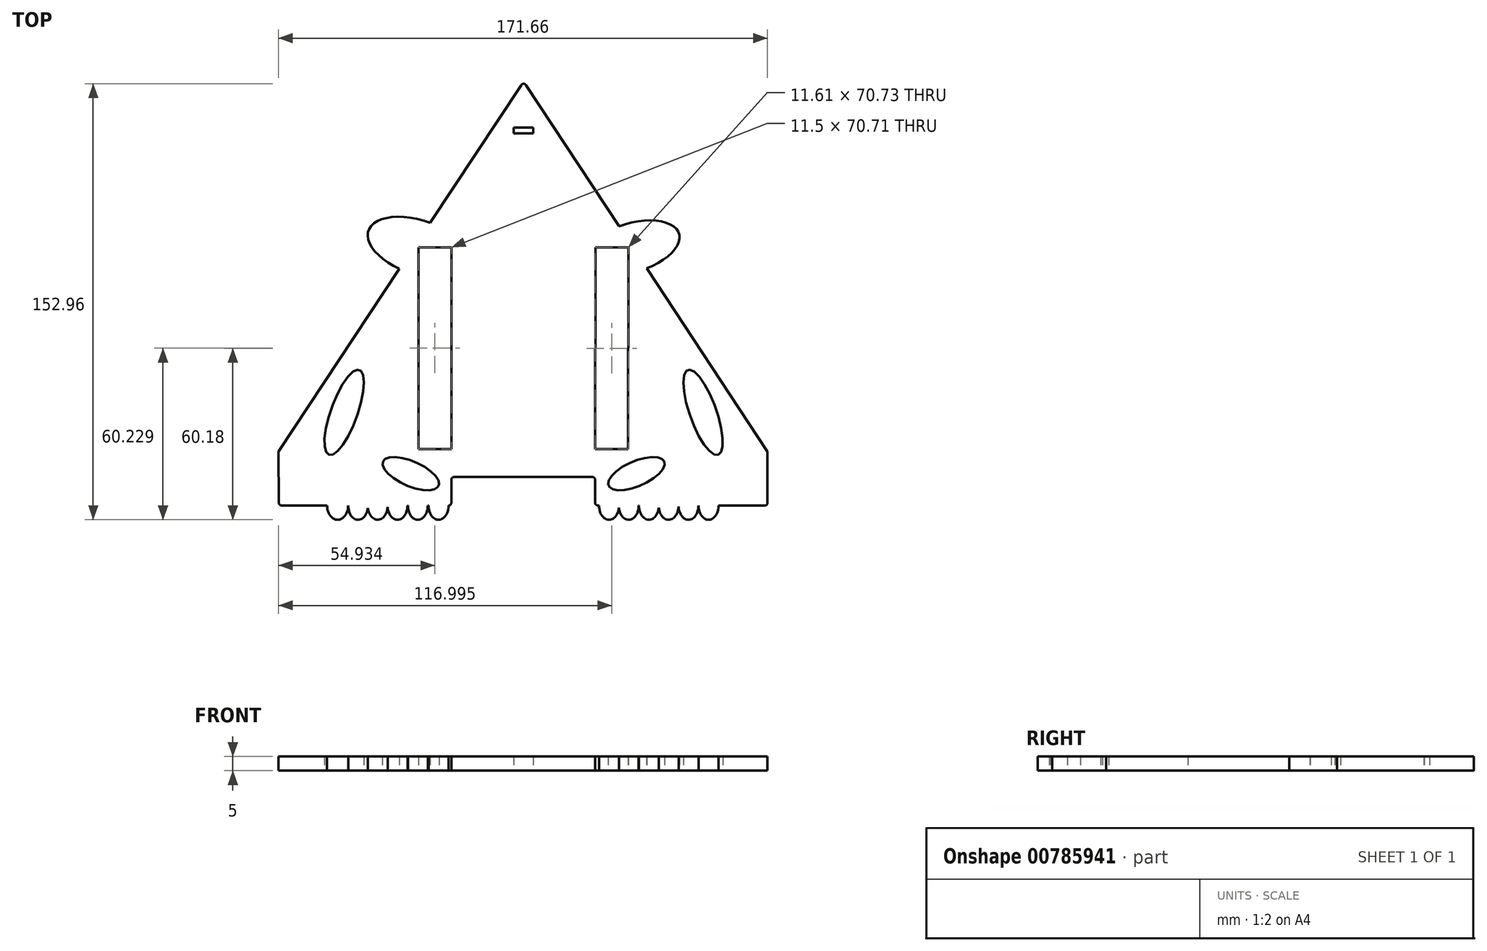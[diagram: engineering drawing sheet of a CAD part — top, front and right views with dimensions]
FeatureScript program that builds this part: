
annotation { "Feature Type Name" : "Feature", "Feature Type Description" : "" }
export const myFeature = defineFeature(function(context is Context, id is Id, definition is map)
    precondition{}
    {
        {
            var Q0;
            Q0=qCreatedBy(makeId("Top.planeOp"),FACE);
            var sketch = newSketch(context, id + "F0", { "sketchPlane" : qUnion([Q0])});
            skPoint(sketch, "E0.0.midPoint", {"position": v(0, -49.5) * mm});
            skPoint(sketch, "E0.cCircle.center.orphan", {"position": v(0, 0) * mm});
            skLineSegment(sketch, "E1", {"start": v(-84.75, -49.5) * mm, "end": v(-54.5, -49.5) * mm});
            skLineSegment(sketch, "E2", {"start": v(84.74, -49.5) * mm, "end": v(26.24, -49.5) * mm});
            skLineSegment(sketch, "E3", {"start": v(25.24, -48.5) * mm, "end": v(25.24, -40.5) * mm});
            skLineSegment(sketch, "E4", {"start": v(24.24, -39.5) * mm, "end": v(-24.24, -39.5) * mm});
            skLineSegment(sketch, "E5", {"start": v(-25.24, -40.5) * mm, "end": v(-25.24, -48.5) * mm});
            skPoint(sketch, "E6.visualSharp", {"position": v(0.12, 99.27) * mm});
            skLineSegment(sketch, "E7", {"start": v(0.95, 98) * mm, "end": v(33.6, 48.5) * mm});
            skLineSegment(sketch, "E8", {"start": v(85.74, -30.56) * mm, "end": v(85.74, -48.5) * mm});
            skLineSegment(sketch, "E9", {"start": v(-85.92, -30.56) * mm, "end": v(-85.75, -48.5) * mm});
            skLineSegment(sketch, "E10", {"start": v(-0.72, 98.01) * mm, "end": v(-33.53, 48.5) * mm});
            skArc(sketch, "E11.filletArc", {"start": v(0.95, 98) * mm, "mid": v(0.12, 98.46) * mm, "end": v(-0.72, 98.01) * mm});
            skPoint(sketch, "E12.visualSharp", {"position": v(85.74, -49.5) * mm});
            skArc(sketch, "E12.filletArc", {"start": v(84.74, -49.5) * mm, "mid": v(85.44, -49.2) * mm, "end": v(85.74, -48.5) * mm});
            skPoint(sketch, "E13.visualSharp", {"position": v(25.24, -49.5) * mm});
            skArc(sketch, "E13.filletArc", {"start": v(25.24, -48.5) * mm, "mid": v(25.53, -49.2) * mm, "end": v(26.24, -49.5) * mm});
            skPoint(sketch, "E14.visualSharp", {"position": v(-85.74, -49.5) * mm});
            skArc(sketch, "E14.filletArc", {"start": v(-85.75, -48.5) * mm, "mid": v(-85.45, -49.21) * mm, "end": v(-84.75, -49.5) * mm});
            skPoint(sketch, "E15.visualSharp", {"position": v(-25.24, -49.5) * mm});
            skArc(sketch, "E15.filletArc", {"start": v(-26.24, -49.5) * mm, "mid": v(-25.53, -49.2) * mm, "end": v(-25.24, -48.5) * mm});
            skPoint(sketch, "E16.visualSharp", {"position": v(25.24, -39.5) * mm});
            skArc(sketch, "E16.filletArc", {"start": v(25.24, -40.5) * mm, "mid": v(24.94, -39.8) * mm, "end": v(24.24, -39.5) * mm});
            skPoint(sketch, "E17.visualSharp", {"position": v(-25.24, -39.5) * mm});
            skArc(sketch, "E17.filletArc", {"start": v(-24.24, -39.5) * mm, "mid": v(-24.94, -39.8) * mm, "end": v(-25.24, -40.5) * mm});
            skEllipticalArc(sketch, "E18", {});
            skEllipticalArc(sketch, "E19", {});
            skEllipticalArc(sketch, "E20", {});
            skEllipticalArc(sketch, "E21", {});
            skEllipticalArc(sketch, "E22", {});
            skEllipticalArc(sketch, "E23", {});
            skPoint(sketch, "E24", {"position": v(-54.44, -49.5) * mm});
            skPoint(sketch, "E25", {"position": v(-54.56, -49.5) * mm});
            skPoint(sketch, "E26", {"position": v(-54.49, -50.37) * mm});
            skLineSegment(sketch, "E27", {"start": v(-54.5, -49.5) * mm, "end": v(-54.5, -50.43) * mm});
            skPoint(sketch, "E28", {"position": v(-47.57, -49.95) * mm});
            skLineSegment(sketch, "E29", {"start": v(-47.58, -50.05) * mm, "end": v(-47.58, -49.5) * mm});
            skLineSegment(sketch, "E30.trimOffspring", {"start": v(-54.44, -49.5) * mm, "end": v(-26.24, -49.5) * mm});
            skEllipticalArc(sketch, "E31", {});
            skEllipticalArc(sketch, "E32", {});
            skEllipticalArc(sketch, "E33", {});
            skEllipticalArc(sketch, "E34", {});
            skEllipticalArc(sketch, "E35", {});
            skEllipticalArc(sketch, "E36", {});
            skPoint(sketch, "E37", {"position": v(26.6, -49.5) * mm});
            skPoint(sketch, "E38", {"position": v(33.53, -49.5) * mm});
            skPoint(sketch, "E39", {"position": v(40.6, -49.5) * mm});
            skPoint(sketch, "E40", {"position": v(40.53, -49.5) * mm});
            skPoint(sketch, "E41", {"position": v(47.6, -49.5) * mm});
            skPoint(sketch, "E42", {"position": v(47.52, -49.5) * mm});
            skPoint(sketch, "E43", {"position": v(54.52, -49.5) * mm});
            skPoint(sketch, "E44", {"position": v(54.5, -49.5) * mm});
            skPoint(sketch, "E45", {"position": v(61.53, -49.5) * mm});
            skPoint(sketch, "E46", {"position": v(61.5, -49.5) * mm});
            skPoint(sketch, "E47", {"position": v(68.53, -49.5) * mm});
            skPoint(sketch, "E48", {"position": v(33.6, -49.5) * mm});
            skLineSegment(sketch, "E49.trimOffspring", {"start": v(-43.32, 33.72) * mm, "end": v(-85.92, -30.56) * mm});
            skEllipticalArc(sketch, "E50", {});
            skLineSegment(sketch, "E51.trimOffspring", {"start": v(43.34, 33.72) * mm, "end": v(85.74, -30.56) * mm});
            skEllipticalArc(sketch, "E52", {});
            skPoint(sketch, "E53", {"position": v(-33.53, 48.5) * mm});
            skPoint(sketch, "E54", {"position": v(-43.32, 33.72) * mm});
            skLineSegment(sketch, "E55", {"start": v(-33.53, 48.5) * mm, "end": v(-31.35, 49.17) * mm});
            skLineSegment(sketch, "E56", {"start": v(33.6, 48.5) * mm, "end": v(33.66, 48.45) * mm});
            skEllipse(sketch, "E57", {"center": v(63.09, -16.83) * mm, "majorRadius": 15.8 * mm, "minorRadius": 4.7 * mm, "majorAxis": v(0.34, -0.94)});
            skEllipse(sketch, "E58", {"center": v(39.7, -38.3) * mm, "majorRadius": 10.66 * mm, "minorRadius": 4.36 * mm, "majorAxis": v(0.92, 0.4)});
            skEllipse(sketch, "E59.MirrorC", {"center": v(-62.85, -16.83) * mm, "majorRadius": 15.8 * mm, "minorRadius": 4.7 * mm, "majorAxis": v(-0.34, -0.94)});
            skEllipse(sketch, "E60.MirrorC", {"center": v(-39.47, -38.3) * mm, "majorRadius": 10.66 * mm, "minorRadius": 4.36 * mm, "majorAxis": v(-0.92, 0.4)});
            skLineSegment(sketch, "E61.trimOffspring", {"start": v(43.32, 33.72) * mm, "end": v(43.34, 33.72) * mm});
            skLineSegment(sketch, "E62", {"start": v(-36.74, 41.09) * mm, "end": v(-36.74, -29.63) * mm});
            skLineSegment(sketch, "E63", {"start": v(-36.74, 41.09) * mm, "end": v(-25.24, 41.09) * mm});
            skLineSegment(sketch, "E64", {"start": v(-36.74, -29.63) * mm, "end": v(-25.24, -29.63) * mm});
            skLineSegment(sketch, "E65", {"start": v(-25.24, -29.63) * mm, "end": v(-25.24, 41.09) * mm});
            skLineSegment(sketch, "E66.MirrorCS", {"start": v(25.27, -29.67) * mm, "end": v(25.38, 41.05) * mm});
            skLineSegment(sketch, "E67.MirrorCS", {"start": v(36.88, 41.03) * mm, "end": v(36.77, -29.69) * mm});
            skLineSegment(sketch, "E68.MirrorCS", {"start": v(36.88, 41.03) * mm, "end": v(25.38, 41.05) * mm});
            skLineSegment(sketch, "E69.MirrorCS", {"start": v(36.77, -29.69) * mm, "end": v(25.27, -29.67) * mm});
            skLineSegment(sketch, "E70", {"start": v(-3.33, 83.04) * mm, "end": v(0, 83.04) * mm});
            skLineSegment(sketch, "E71", {"start": v(-3.33, 83.04) * mm, "end": v(-3.33, 81.04) * mm});
            skLineSegment(sketch, "E72", {"start": v(-3.33, 81.04) * mm, "end": v(0, 81.04) * mm});
            skLineSegment(sketch, "E73.MirrorCS", {"start": v(3.54, 83.04) * mm, "end": v(0.21, 83.04) * mm});
            skLineSegment(sketch, "E74.MirrorCS", {"start": v(3.54, 81.04) * mm, "end": v(0.2, 81.04) * mm});
            skLineSegment(sketch, "E75.MirrorCS", {"start": v(3.54, 83.04) * mm, "end": v(3.54, 81.04) * mm});
            skLineSegment(sketch, "E76", {"start": v(0, 81.04) * mm, "end": v(0.2, 81.04) * mm});
            skLineSegment(sketch, "E77", {"start": v(0, 83.04) * mm, "end": v(0.21, 83.04) * mm});
            const initialGuessF0  = {"E18": [-0.029729247093200684, -0.0495000034570694, 0, -1, 0.005, 0.0035, 4.71238898038469, 1.570801617782231], "E19": [-0.03698873519897461, -0.0495000034570694, 0, -1, 0.005, 0.0035, 4.71238898038469, 1.5707963267948966], "E20": [-0.044100072234869, -0.0495000034570694, 0, -1, 0.005, 0.0035, 4.822721470064113, 1.5707963267948966], "E21": [-0.05105750903492189, -0.0495000034570694, 0, -1, 0.005, 0.0035, 4.899477820012888, 1.4604638371154721], "E22": [-0.05793535813684248, -0.0495000034570694, 0, -1, 0.005, 0.0035, 4.71238898038469, 1.3953355132787328], "E23": [-0.06513869762420654, -0.0495000034570694, 0, -1, 0.005, 0.0037033394873640557, 4.71238898038469, 1.5707963267948966], "E31": [0.030106185004115105, -0.04950000345706941, 0, -1, 0.005, 0.0035, 4.71238898038469, 1.5707963267948966], "E32": [0.037028003484010696, -0.04950000345706941, 0, -1, 0.005, 0.0035, 4.71238898038469, 1.5707963267948966], "E33": [0.044100940227508545, -0.04950000345706941, 0, -1, 0.005, 0.0035, 4.71238898038469, 1.5707963267948966], "E34": [0.05102432146668434, -0.04950000345706941, 0, -1, 0.005, 0.0035, 4.71238898038469, 1.5707963267948966], "E35": [0.05800028517842293, -0.04950000345706941, 0, -1, 0.005, 0.0035, 4.71238898038469, 1.5707963267948966], "E36": [0.06503187119960785, -0.04950000345706941, 0, -1, 0.005, 0.0035, 4.71238898038469, 1.5707963267948966], "E50": [-0.03673652096247923, 0.04108645766973406, 0.9491522126047598, -0.31481753017817954, 0.018534346020662177, 0.009462294803832105, 1.4319341267225272, 4.495986690844154], "E52": [0.03848833608708242, 0.041086457669728384, -0.9600526165022497, -0.2798195374651036, 0.016875, 0.008521082131865629, 1.7240567735104766, 4.865276969991962]};
            skSetInitialGuess(sketch, initialGuessF0);
            skSolve(sketch);
        }
        {
            var Q0;
            Q0=qSketchRegion(id+"F0",true);
            var Q1;
            Q1=qSketchRegion(id+"FPg5yT2tUSxsPf8_0",true);
            extrude(context, id + "F1", {"entities" : qUnion([Q0, Q1]), "depth" : 5 * mm, "offsetDistance" : 25 * mm});
        }
    });
